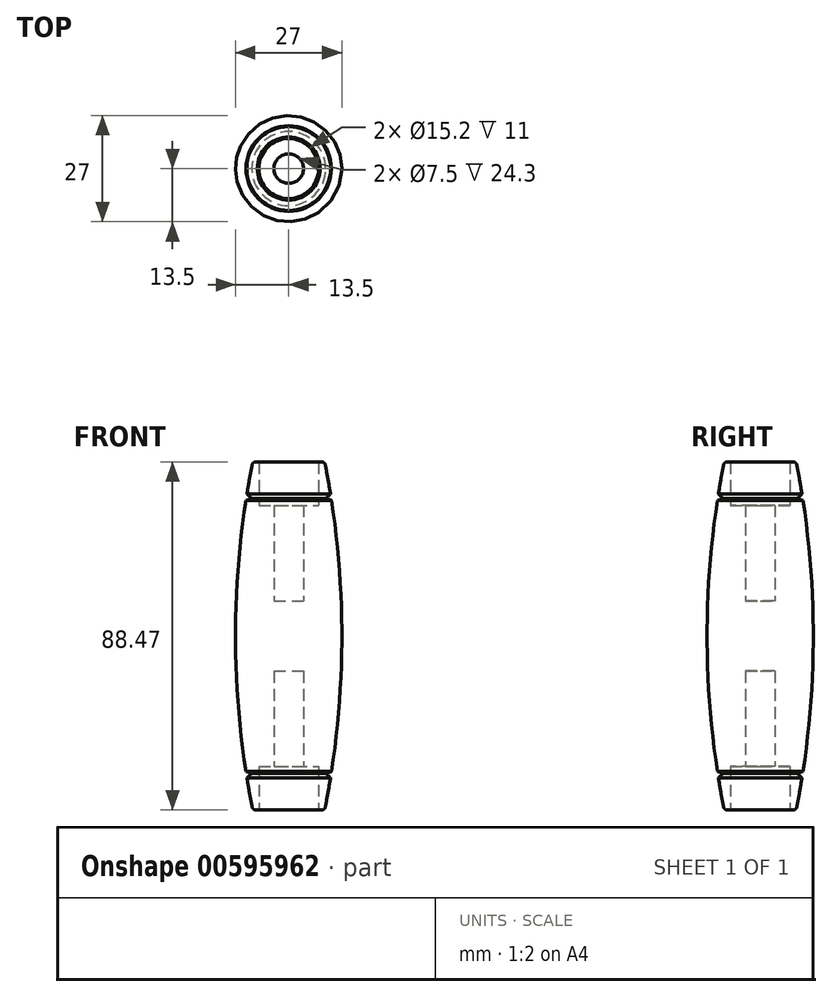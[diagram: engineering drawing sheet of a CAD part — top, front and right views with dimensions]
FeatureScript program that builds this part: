
annotation { "Feature Type Name" : "Feature", "Feature Type Description" : "" }
export const myFeature = defineFeature(function(context is Context, id is Id, definition is map)
    precondition{}
    {
        {
            var Q0;
            Q0=qCreatedBy(makeId("Front.planeOp"),FACE);
            var sketch = newSketch(context, id + "F0", { "sketchPlane" : qUnion([Q0])});
            skLineSegment(sketch, "E0", {"start": v(0, 0) * mm, "end": v(0, 88.37) * mm, "construction": true});
            skArc(sketch, "E1", {"start": v(9, -0.82) * mm, "mid": v(13.5, 44.18) * mm, "end": v(9, 89.18) * mm});
            skLineSegment(sketch, "E2", {"start": v(-213.5, 44.18) * mm, "end": v(0, 44.18) * mm, "construction": true});
            skLineSegment(sketch, "E3", {"start": v(13.5, 44.18) * mm, "end": v(13.5, 17.37) * mm, "construction": true});
            skLineSegment(sketch, "E4", {"start": v(0, 0) * mm, "end": v(0, 88.37) * mm});
            skLineSegment(sketch, "E5", {"start": v(9, 89.18) * mm, "end": v(-10.02, 89.18) * mm, "construction": true});
            skLineSegment(sketch, "E6", {"start": v(9, -0.82) * mm, "end": v(-18, -0.82) * mm, "construction": true});
            skLineSegment(sketch, "E7", {"start": v(0, 88.37) * mm, "end": v(33.92, 88.37) * mm, "construction": true});
            skLineSegment(sketch, "E8", {"start": v(0, 0) * mm, "end": v(42, 0) * mm, "construction": true});
            skLineSegment(sketch, "E9", {"start": v(0, 88.37) * mm, "end": v(8, 88.37) * mm});
            skLineSegment(sketch, "E10", {"start": v(8, 88.37) * mm, "end": v(9, 89.18) * mm});
            skLineSegment(sketch, "E11", {"start": v(0, 0) * mm, "end": v(8, 0) * mm});
            skLineSegment(sketch, "E12", {"start": v(8, 0) * mm, "end": v(9, -0.82) * mm});
            skSolve(sketch);
        }
        {
            var Q0;
            Q0=makeQuery(id+"F0.imprint","IMPRINT",FACE,{"disambiguationData":[TD([[makeQuery(id+"F0.imprint","IMPRINT",EDGE,{"derivedFrom":sQuery(id+"F0.wireOp",EDGE,"E1")}),1.0]])]});
            var Q1;
            Q1=sQuery(id+"F0.wireOp",EDGE,"E4");
            revolve(context, id + "F1", {"entities" : qUnion([Q0]), "axis" : qUnion([Q1]), "revolveType" : RevolveType.FULL});
        }
        {
            var Q0;
            Q0=makeQuery(id+"F1.opRevolve","SWEPT_EDGE",EDGE,{"disambiguationData":[OSD([sQuery(id+"F0.wireOp",EDGE,"E1"),sQuery(id+"F0.wireOp",EDGE,"oIb8xYxR-XwdV-IQJ0-qUSZ-DkgYWBHBJ82f")])]});
            var Q1;
            Q1=makeQuery(id+"F1.opRevolve","SWEPT_EDGE",EDGE,{"disambiguationData":[OSD([sQuery(id+"F0.wireOp",EDGE,"E1"),sQuery(id+"F0.wireOp",EDGE,"766e9889-5059-467a-8efe-476706b1f5470.MirrorCS")])]});
            fillet(context, id + "F2", {"entities" : qUnion([Q0, Q1]), "radius" : 1 * mm, "tangentPropagation" : true, "allowEdgeOverflow" : false});
        }
        {
            var Q0;
            Q0=qCreatedBy(makeId("Front.planeOp"),FACE);
            var sketch = newSketch(context, id + "F3", { "sketchPlane" : qUnion([Q0])});
            skArc(sketch, "E13", {"start": v(-8.04, 89.02) * mm, "mid": v(0, 88.37) * mm, "end": v(8.04, 89.02) * mm, "construction": true});
            skArc(sketch, "E14", {"start": v(8.04, -0.65) * mm, "mid": v(0, 0) * mm, "end": v(-8.04, -0.65) * mm, "construction": true});
            skLineSegment(sketch, "E15", {"start": v(8.04, 89.02) * mm, "end": v(8.04, -0.65) * mm, "construction": true});
            skLineSegment(sketch, "E16", {"start": v(8.04, 44.18) * mm, "end": v(-31.5, 44.18) * mm, "construction": true});
            skLineSegment(sketch, "E17", {"start": v(14.73, 83.85) * mm, "end": v(9.4, 79.14) * mm});
            skLineSegment(sketch, "E18", {"start": v(9.4, 79.14) * mm, "end": v(17.61, 76.39) * mm});
            skLineSegment(sketch, "E19", {"start": v(14.73, 83.85) * mm, "end": v(17.61, 76.39) * mm});
            skLineSegment(sketch, "E20.MirrorCS", {"start": v(14.73, 4.52) * mm, "end": v(9.4, 9.23) * mm});
            skLineSegment(sketch, "E21.MirrorCS", {"start": v(9.4, 9.23) * mm, "end": v(17.61, 11.98) * mm});
            skLineSegment(sketch, "E22.MirrorCS", {"start": v(14.73, 4.52) * mm, "end": v(17.61, 11.98) * mm});
            skLineSegment(sketch, "E23", {"start": v(0, 0) * mm, "end": v(0, 55.62) * mm, "construction": true});
            skSolve(sketch);
        }
        {
            var Q0;
            Q0=qSketchRegion(id+"F3",true);
            var Q1;
            Q1=sQuery(id+"F3.wireOp",EDGE,"E23");
            revolve(context, id + "F4", {"operationType" : NewBodyOperationType.REMOVE, "entities" : qUnion([Q0]), "axis" : qUnion([Q1]), "revolveType" : RevolveType.FULL, "oppositeDirection" : true});
        }
        {
            var Q0;
            Q0=qCreatedBy(makeId("Front.planeOp"),FACE);
            var sketch = newSketch(context, id + "F5", { "sketchPlane" : qUnion([Q0])});
            skLineSegment(sketch, "E24", {"start": v(0, 53.07) * mm, "end": v(3.75, 53.07) * mm});
            skLineSegment(sketch, "E25", {"start": v(3.75, 53.07) * mm, "end": v(3.75, 77.37) * mm});
            skLineSegment(sketch, "E26", {"start": v(3.75, 77.37) * mm, "end": v(7.6, 77.37) * mm});
            skLineSegment(sketch, "E27", {"start": v(7.6, 77.37) * mm, "end": v(7.6, 88.37) * mm});
            skLineSegment(sketch, "E28", {"start": v(7.6, 88.37) * mm, "end": v(0, 88.37) * mm});
            skLineSegment(sketch, "E29", {"start": v(0, 88.37) * mm, "end": v(0, 53.07) * mm});
            skLineSegment(sketch, "E30", {"start": v(0, 0) * mm, "end": v(18.19, 0) * mm, "construction": true});
            skLineSegment(sketch, "E31", {"start": v(0, -0.82) * mm, "end": v(18.27, -0.82) * mm, "construction": true});
            skLineSegment(sketch, "E32.0", {"start": v(10.87, 78.65) * mm, "end": v(-10.87, 78.65) * mm, "construction": true});
            skLineSegment(sketch, "E33.0", {"start": v(10.87, 9.72) * mm, "end": v(-10.87, 9.72) * mm, "construction": true});
            skLineSegment(sketch, "E34", {"start": v(0, 78.65) * mm, "end": v(0, 9.72) * mm, "construction": true});
            skLineSegment(sketch, "E35", {"start": v(0, 44.18) * mm, "end": v(42.7, 44.18) * mm, "construction": true});
            skLineSegment(sketch, "E36.MirrorCS", {"start": v(0, 35.3) * mm, "end": v(3.75, 35.3) * mm});
            skLineSegment(sketch, "E37.MirrorCS", {"start": v(3.75, 35.3) * mm, "end": v(3.75, 11) * mm});
            skLineSegment(sketch, "E38.MirrorCS", {"start": v(3.75, 11) * mm, "end": v(7.6, 11) * mm});
            skLineSegment(sketch, "E39.MirrorCS", {"start": v(7.6, 11) * mm, "end": v(7.6, 0) * mm});
            skLineSegment(sketch, "E40.MirrorCS", {"start": v(0, 0) * mm, "end": v(0, 35.3) * mm});
            skLineSegment(sketch, "E41.MirrorCS", {"start": v(7.6, 0) * mm, "end": v(0, 0) * mm});
            skSolve(sketch);
        }
        {
            var Q0;
            Q0 = qSketchRegion(id + "F5", true);
            var Q1;
            Q1=sQuery(id+"F5.wireOp",EDGE,"E34");
            revolve(context, id + "F6", {"operationType" : NewBodyOperationType.REMOVE, "entities" : qUnion([Q0]), "axis" : qUnion([Q1]), "revolveType" : RevolveType.FULL, "oppositeDirection" : true});
        }
    });
